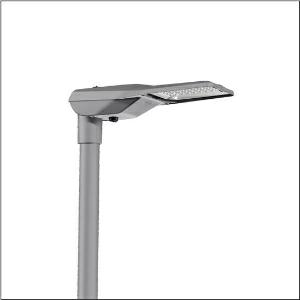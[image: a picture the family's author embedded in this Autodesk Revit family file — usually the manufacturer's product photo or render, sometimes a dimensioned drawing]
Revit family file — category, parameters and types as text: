
# Revit family: streetlight_sl_21_iq_mini___st0_8a_5xe2c31y08jb_7a77
name_source: partatom
category: Lighting Fixtures
units: mm (PartAtom-declared; Revit-internal decimal feet)

## family parameters
Cut with Voids When Loaded = No
Host = Face
Light Source = No
Part Type = Normal
Room Calculation Point = No
Round Connector Dimension = Use Diameter
Shared = No

## types (1)
- --- (1 x LED, 11210 lm, 72.5 W, 3000K)
    Apparent Load = 73 VA
    CIE Flux Codes = 41 75 97 100 100
    Color Rendering = 70
    Color Temperature = 3000K
    Default Elevation = 1800 mm
    Description = Streetlight SL 21 iQ mini, mast luminaire, primary light control with lens, of PMMA, primary optical cover: cover, of toughened safety glass, transparent, light distribution: ST0.8a, light emission: direct distribution, primary light characteristic: asymmetric, installation type: post-top, side-entry, LED, High Power LED, rated luminous flux: 11.210lm, luminous efficacy: 155lm/W, light colour: 730, colour temperature: 3000K, control: presetting dimming logarithmic, Street-Remote, Auto-Match, Temp-Guard, Lumen-Switch, Night-Set, Smart-Wire, Light-Fading, Desk-Remote (wireless, voltage-free reading and setting of iQ features in the workshop via application-optimized NFC function/RFID function), optimised constant luminous flux control (CLO 2.0), mains connection: 220..240V, AC, 50/60Hz, start of lifetime: 73W, end of service life: 76W, reduction: 33W, luminaire housing, of diecast aluminium, powder-coated, Siteco® metallic grey (DB 702S), corrosivity category C5 mid according to DIN EN ISO 12944, please order mast flange separately, inclination adjustable: 0°, 5°, 10°, 15°, sealing non-destructively replaceable, multi-level sealing system, length: 628mm, width: 235mm, height: 110mm, mast flange for spigot size: 42mm (side-entry): 5XC10008XM4, 60/48mm (side-entry/post-top): 5XC10108XM2, 76/60mm (side-entry/post-top): 5XC10108XM1, Smart Interface below and above, protection rating (complete): IP66, insulation class (complete): insulation class II (safety insulation), certification: CE, ENEC, ENEC+, VDE, impact resistance: IK09, permissible operating ambient temperature for outdoor applications: -40..+50°C, standard-compliant lighting for roads and squares, packaging unit: 1 piece

Light Distribution: ST0.8a
    Height = 110 mm
    Lamp = 1 x LED
    Lamp Light Flux = 11210 lm
    Lamp Power = 72.5 W
    Lamp count = 1
    Length = 625 mm
    Luminous efficacy = 155 lm/W
    Manufacturer = Siteco
    ModVariant = No
    Model = 5XE2C31Y08JB
    Number of Poles = 1
    OnlyDefault = Yes
    Power Factor = 1
    Product Name = Streetlight SL 21 iQ mini | ST0.8a
    Product group = mast luminaire | pylon top
    ProductGroupID = 6100
    Protection Class = Protection class II
    Protection Degree = IP 66
    RLX_Detail_Level = 1
    RLX_Emergency_Light_Flux = 0 lm
    RLX_Emergency_Type = 0
    RLX_Emergency_Type_DB = No
    RlxData = <blob elided: 92769 chars, md5=f48190da>
    Socket = socket
    Standby Power = 0 W
    System Light Flux = 11210 lm
    System Power = 73 W
    Type Comments = factory setting: luminous flux: 100 % | dim-lin: 254 | 755 mA
    Type Image = l_1003514.jpg
    URL = http://relux.com
    VarID = @adj_043271
    Voltage = 0 V
    Weight = 0.00 kg
    Width = 234 mm

## geometry (parser evidence)
native form markers: Blend x4, Sweep x12
no freeform markers — native parametric forms only
